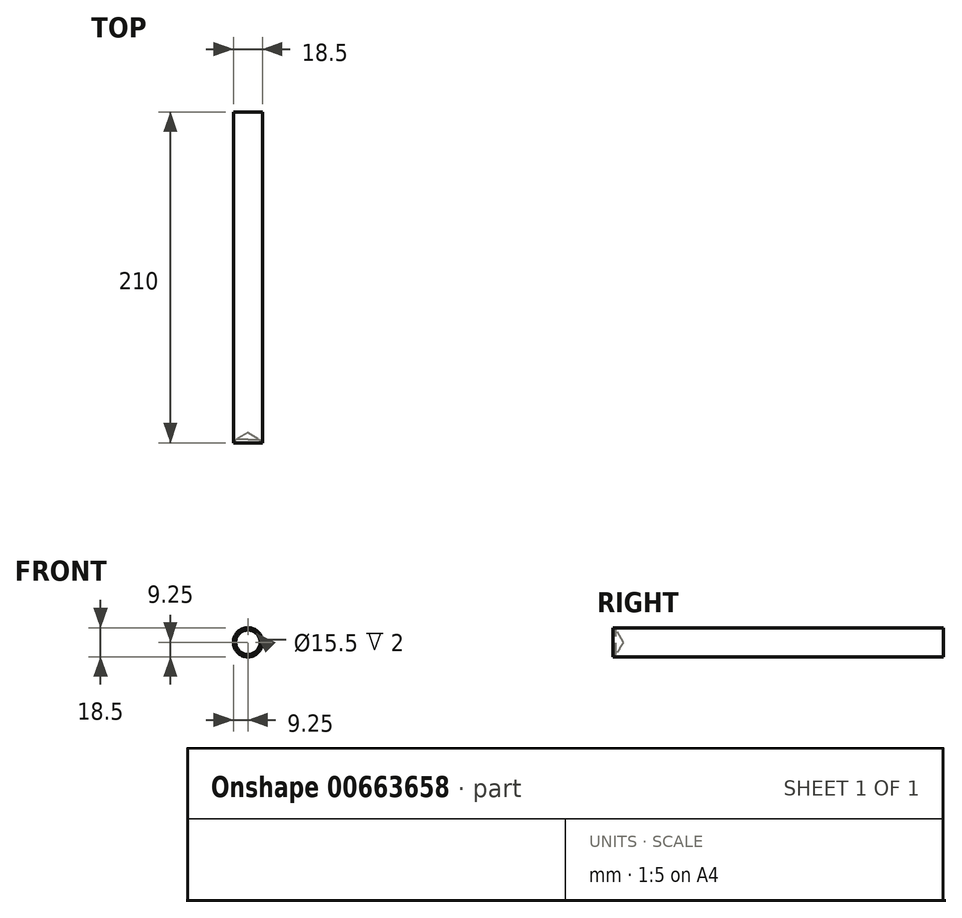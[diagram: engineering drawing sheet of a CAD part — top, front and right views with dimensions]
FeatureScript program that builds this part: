
annotation { "Feature Type Name" : "Feature", "Feature Type Description" : "" }
export const myFeature = defineFeature(function(context is Context, id is Id, definition is map)
    precondition{}
    {
        {
            var Q0;
            Q0=qCreatedBy(makeId("Front.planeOp"),FACE);
            var sketch = newSketch(context, id + "F0", { "sketchPlane" : qUnion([Q0])});
            skCircle(sketch, "E0", {"center": v(0, 0) * mm, "radius": 9.25 * mm});
            skCircle(sketch, "E1.0", {"center": v(0, 0) * mm, "radius": 7.75 * mm, "construction": true});
            skSolve(sketch);
        }
        {
            var Q0;
            Q0=qSketchRegion(id+"F0",true);
            extrude(context, id + "F1", {"entities" : qUnion([Q0]), "depth" : 210 * mm, "offsetDistance" : 25 * mm});
        }
        {
            var Q0;
            Q0=makeQuery(id+"F1.opExtrude","CAP_FACE",FACE,{"disambiguationData":[OSD([sQuery(id+"F0.wireOp",EDGE,"E0")])],"isStart":false});
            var sketch = newSketch(context, id + "F2", { "sketchPlane" : qUnion([Q0])});
            skPoint(sketch, "E2", {"position": v(0, 0) * mm});
            skSolve(sketch);
        }
        {
            var Q0;
            Q0=sQuery(id+"F2.wireOp",VERTEX,"E2");
            var Q1;
            Q1=makeQuery(id+"F1.opExtrude","SWEPT_BODY",BODY,{"disambiguationData":[OSD([sQuery(id+"F0.wireOp",EDGE,"E0")])]});
            hole(context, id + "F3", {"style" : HoleStyle.SIMPLE, "endStyle" : HoleEndStyle.BLIND, "holeDiameter" : 15.5 * mm, "majorDiameter" : 5 * mm, "holeDepth" : 2 * mm, "isTappedThrough" : true, "tappedDepth" : 12 * mm, "tapClearance" : 3, "startFromSketch" : true, "locations" : qUnion([Q0]), "scope" : qUnion([Q1])});
        }
        {
            var Q0;
            Q0=makeQuery(id+"F1.opExtrude","CAP_FACE",FACE,{"disambiguationData":[OSD([sQuery(id+"F0.wireOp",EDGE,"E0")])],"isStart":false});
            var Q1;
            Q1=makeQuery(id+"F1.opExtrude","CAP_FACE",FACE,{"disambiguationData":[OSD([sQuery(id+"F0.wireOp",EDGE,"E0")])],"isStart":true});
            cPlane(context, id + "F4", {"entities" : qUnion([Q0, Q1]), "cplaneType" : CPlaneType.MID_PLANE, "offset" : 25 * mm, "width" : 150 * mm, "height" : 150 * mm});
        }
    });
